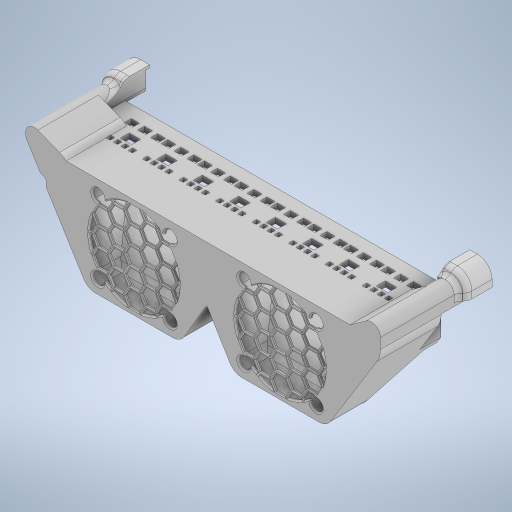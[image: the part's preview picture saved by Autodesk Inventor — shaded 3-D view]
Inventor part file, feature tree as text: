
AUTODESK INVENTOR PART (.ipt)
format: ipt  version: 2023.1 (Build 271208000, 208)  size: 5,121,536 bytes
history: native  units: mm
features: reference x62, projected_geometry x51, extrude x44, sketch x44, delete_face x35, other x18, fillet x13, move_body x9, direct_edit x7, chamfer x7, hole x1
ambient origin geometry x8: Origin, YZ Plane, XZ Plane, XY Plane, X Axis, Y Axis, Z Axis, Center Point
bodies: Volumenkörper1 (feature_tree)
feature tree (291):
  extrude  "Extrusion1"  Depth=2.6mm
  extrude  "Extrusion2"  Depth=0.4195mm
  extrude  "Extrusion3"  Depth=8.0mm
  extrude  "Extrusion4"  Depth=2.6mm
  extrude  "Extrusion5"  Depth=0.482959mm
  extrude  "Extrusion6"  Depth=0.4mm
  delete_face  "Fläche löschen1"
  extrude  "Extrusion7"  Depth=9.8mm TaperAngle=0.0deg
  extrude  "Extrusion8"  Depth=3.0mm TaperAngle=0.0deg
  extrude  "Extrusion9"  Depth=40.0mm
  delete_face  "Fläche löschen2"
  delete_face  "Fläche löschen3"
  delete_face  "Fläche löschen4"
  extrude  "Extrusion10"  Depth=40.0mm
  delete_face  "Fläche löschen5"
  delete_face  "Fläche löschen6"
  delete_face  "Fläche löschen7"
  extrude  "Extrusion11"  Depth=12.004mm
  delete_face  "Fläche löschen8"
  extrude  "Extrusion12"  Depth=12.131mm
  delete_face  "Fläche löschen9"
  delete_face  "Fläche löschen10"
  delete_face  "Fläche löschen11"
  delete_face  "Fläche löschen12"
  extrude  "Extrusion13"  Depth=2.0mm
  extrude  "Extrusion14"  Depth=12.0mm TaperAngle=0.0deg
  delete_face  "Fläche löschen13"
  direct_edit  "Direktbearbeitung1"
  extrude  "Extrusion15"  Depth=0.2mm
  extrude  "Extrusion16"  Depth=0.2mm
  chamfer  "Fase1"  Distance=12.0mm
  delete_face  "Fläche löschen14"
  delete_face  "Fläche löschen15"
  chamfer  "Fase2"  Distance=10.0mm
  delete_face  "Fläche löschen16"
  chamfer  "Fase3"  Distance=10.0mm
  chamfer  "Fase4"  [1 undecoded]
  extrude  "Extrusion17"  Depth=10.0mm TaperAngle=0.0deg
  extrude  "Extrusion18"  Depth=1.2mm
  delete_face  "Fläche löschen17"
  extrude  "Extrusion19"  Depth=54.3755mm
  delete_face  "Fläche löschen18"
  delete_face  "Fläche löschen19"
  extrude  "Extrusion20"  Depth=10.0mm TaperAngle=0.0deg
  extrude  "Extrusion21"  Depth=10.0mm
  fillet  "Rundung1"  Radius=2.044525mm
  fillet  "Rundung2"  Radius=2.044525mm
  delete_face  "Fläche löschen20"
  delete_face  "Fläche löschen21"
  extrude  "Extrusion22"  Depth=5.0mm TaperAngle=0.0deg
  delete_face  "Fläche löschen22"
  extrude  "Extrusion23"  Depth=40.4mm
  extrude  "Extrusion24"  Depth=40.4mm
  delete_face  "Fläche löschen23"
  extrude  "Extrusion25"  Depth=2.0mm
  delete_face  "Fläche löschen24"
  extrude  "Extrusion26"  Depth=2.0mm
  delete_face  "Fläche löschen25"
  extrude  "Extrusion27"  Depth=2.0mm
  delete_face  "Fläche löschen26"
  direct_edit  "Direktbearbeitung2"
  extrude  "Extrusion28"  TaperAngle=30.0deg  [1 undecoded]
  extrude  "Extrusion29"  TaperAngle=30.0deg  [1 undecoded]
  extrude  "Extrusion30"  TaperAngle=45.0deg  [1 undecoded]
  extrude  "Extrusion31"  Depth=2.0mm
  extrude  "Extrusion32"  Depth=2.0mm
  extrude  "Extrusion33"  Depth=2.0mm
  direct_edit  "Direktbearbeitung3"
  delete_face  "Fläche löschen27"
  extrude  "Extrusion34"  Depth=2.0mm
  delete_face  "Fläche löschen28"
  delete_face  "Fläche löschen29"
  delete_face  "Fläche löschen30"
  delete_face  "Fläche löschen31"
  fillet  "Rundung3"  Radius=4.1mm
  extrude  "Extrusion35"  Depth=2.0mm
  chamfer  "Fase5"  Distance=11.1mm
  extrude  "Extrusion36"  Depth=2.0mm
  delete_face  "Fläche löschen32"
  delete_face  "Fläche löschen33"
  direct_edit  "Direktbearbeitung4"
  extrude  "Extrusion37"  Depth=2.0mm
  fillet  "Rundung4"  Radius=13.5mm
  fillet  "Rundung5"  Radius=16.4mm
  fillet  "Rundung6"  Radius=15.2mm
  fillet  "Rundung7"  Radius=8.2mm
  fillet  "Rundung8"  Radius=7.0mm
  fillet  "Rundung9"  Radius=0.0mm
  chamfer  "Fase7"  Distance=1.2mm
  extrude  "Extrusion38"  Depth=2.0mm
  sketch  "Skizze44"  dims[d78=10.0mm d79=0.0mm d80=10.0mm d81=0.0mm]
  extrude  "Extrusion39"  Depth=2.0mm
  extrude  "Extrusion40"  Depth=2.0mm
  direct_edit  "Direktbearbeitung5"
  chamfer  "Fase8"  Distance=17.6mm
  fillet  "Rundung10"  Radius=19.7279mm
  delete_face  "Fläche löschen34"
  delete_face  "Fläche löschen35"
  fillet  "Rundung11"  Radius=19.3mm
  fillet  "Rundung12"  Radius=12.3mm
  extrude  "Extrusion41"  Depth=2.0mm
  extrude  "Extrusion42"  Depth=2.0mm
  direct_edit  "Direktbearbeitung6"
  hole  "Bohrung1"  [1 undecoded]
  direct_edit  "Direktbearbeitung7"
  extrude  "Extrusion43"  Depth=2.0mm
  fillet  "Rundung13"  Radius=5.3mm
  extrude  "Extrusion44"  Depth=2.0mm
  sketch  "Skizze1"  dims[d0=8.8mm d1=0.0mm d4=2.6mm]
  reference  "Referenz1"
  reference  "Referenz2"
  reference  "Referenz3"
  reference  "Referenz4"
  reference  "Referenz5"
  reference  "Referenz6"
  reference  "Referenz7"
  reference  "Referenz8"
  reference  "Referenz9"
  reference  "Referenz10"
  reference  "Referenz11"
  reference  "Referenz12"
  reference  "Referenz13"
  sketch  "Skizze2"  dims[d5=0.4195mm d6=0.4195mm]
  reference  "Referenz14"
  reference  "Referenz15"
  projected_geometry  "Projizierte Kontur1"
  reference  "Referenz16"
  reference  "Referenz17"
  reference  "Referenz18"
  reference  "Referenz19"
  sketch  "Skizze3"  dims[d7=5.999988mm d8=8.0mm]
  projected_geometry  "Projizierte Kontur2"
  reference  "Referenz20"
  reference  "Referenz21"
  reference  "Referenz22"
  reference  "Referenz23"
  reference  "Referenz24"
  reference  "Referenz25"
  sketch  "Skizze4"  dims[d9=8.0mm d10=2.6mm]
  projected_geometry  "Projizierte Kontur3"
  reference  "Referenz26"
  reference  "Referenz27"
  reference  "Referenz28"
  reference  "Referenz29"
  sketch  "Skizze5"  dims[d11=0.482959mm d12=0.482959mm]
  projected_geometry  "Projizierte Kontur4"
  projected_geometry  "Projizierte Kontur5"
  projected_geometry  "Projizierte Kontur6"
  projected_geometry  "Projizierte Kontur7"
  sketch  "Skizze7"  dims[d13=0.4mm d14=0.4mm]
  projected_geometry  "Projizierte Kontur8"
  reference  "Referenz30"
  reference  "Referenz31"
  sketch  "Skizze9"  dims[d15=2.6mm d16=9.8mm d17=0.0mm]
  projected_geometry  "Projizierte Kontur9"
  reference  "Referenz34"
  reference  "Referenz35"
  reference  "Referenz36"
  sketch  "Skizze10"  dims[d18=0.4mm d19=3.0mm d20=0.0mm]
  projected_geometry  "Projizierte Kontur10"
  projected_geometry  "Projizierte Kontur11"
  sketch  "Skizze11"  dims[d21=40.0mm d22=40.0mm]
  projected_geometry  "Projizierte Kontur12"
  sketch  "Skizze13"  dims[d23=40.0mm d24=40.0mm]
  projected_geometry  "Projizierte Kontur13"
  sketch  "Skizze14"  dims[d25=12.004mm d26=12.004mm]
  projected_geometry  "Projizierte Kontur14"
  reference  "Referenz37"
  reference  "Referenz38"
  reference  "Referenz39"
  reference  "Referenz40"
  sketch  "Skizze15"  dims[d27=12.131mm d28=12.131mm]
  projected_geometry  "Projizierte Kontur15"
  sketch  "Skizze16"  dims[d29=2.0mm d30=0.492mm]
  projected_geometry  "Projizierte Kontur16"
  projected_geometry  "Projizierte Kontur17"
  sketch  "Skizze17"  dims[d31=0.492mm d32=12.0mm d33=0.0mm]
  projected_geometry  "Projizierte Kontur18"
  reference  "Referenz41"
  reference  "Referenz42"
  reference  "Referenz43"
  reference  "Referenz44"
  reference  "Referenz45"
  sketch  "Skizze18"  dims[d34=0.2mm d35=0.2mm]
  projected_geometry  "Projizierte Kontur19"
  sketch  "Skizze20"  dims[d36=0.2mm d37=0.2mm]
  projected_geometry  "Projizierte Kontur20"
  projected_geometry  "Projizierte Kontur21"
  sketch  "Skizze21"  dims[d38=0.2mm]
  sketch  "Skizze22"  dims[d39=0.2mm]
  projected_geometry  "Projizierte Kontur22"
  projected_geometry  "Projizierte Kontur23"
  sketch  "Skizze23"  dims[d40=0.2mm]
  sketch  "Skizze24"  dims[d41=1.6mm]
  projected_geometry  "Projizierte Kontur24"
  sketch  "Skizze25"  dims[d42=1.6mm]
  projected_geometry  "Projizierte Kontur25"
  projected_geometry  "Projizierte Kontur26"
  sketch  "Skizze27"  dims[d43=1.6mm]
  projected_geometry  "Projizierte Kontur28"
  sketch  "Skizze28"  dims[d44=1.6mm]
  projected_geometry  "Projizierte Kontur29"
  projected_geometry  "Projizierte Kontur30"
  projected_geometry  "Projizierte Kontur31"
  sketch  "Skizze29"  dims[d45=1.6mm]
  projected_geometry  "Projizierte Kontur32"
  sketch  "Skizze30"  dims[d46=1.6mm]
  projected_geometry  "Projizierte Kontur33"
  sketch  "Skizze31"  dims[d47=1.6mm]
  projected_geometry  "Projizierte Kontur34"
  sketch  "Skizze32"  dims[d48=1.6mm d49=12.0mm d50=0.0mm]
  sketch  "Skizze33"  dims[d51=1.0mm]
  projected_geometry  "Projizierte Kontur35"
  sketch  "Skizze34"  dims[d52=4.2mm]
  projected_geometry  "Projizierte Kontur36"
  projected_geometry  "Projizierte Kontur37"
  sketch  "Skizze35"  dims[d53=1.2mm d54=10.0mm d55=0.0mm]
  projected_geometry  "Projizierte Kontur38"
  projected_geometry  "Projizierte Kontur39"
  sketch  "Skizze36"  dims[d61=1.6mm]
  projected_geometry  "Projizierte Kontur40"
  sketch  "Skizze37"  dims[d62=0.292mm]
  projected_geometry  "Projizierte Kontur41"
  projected_geometry  "Projizierte Kontur42"
  sketch  "Skizze38"  dims[d63=0.292mm]
  projected_geometry  "Projizierte Kontur43"
  sketch  "Skizze39"  dims[d64=1.2mm]
  projected_geometry  "Projizierte Kontur44"
  projected_geometry  "Projizierte Kontur45"
  sketch  "Skizze40"  dims[d65=1.2mm d66=10.0mm d67=0.0mm d68=0.0mm d69=0.0mm]
  projected_geometry  "Projizierte Kontur46"
  sketch  "Skizze41"  dims[d70=10.0mm d71=0.0mm d72=10.0mm d73=0.0mm]
  projected_geometry  "Projizierte Kontur47"
  sketch  "Skizze42"  dims[d74=0.0mm d75=1.2mm]
  projected_geometry  "Projizierte Kontur48"
  sketch  "Skizze43"  dims[d76=108.751mm d77=54.3755mm]
  projected_geometry  "Projizierte Kontur49"
  reference  "Referenz47"
  reference  "Referenz48"
  reference  "Referenz49"
  reference  "Referenz50"
  reference  "Referenz51"
  reference  "Referenz52"
  reference  "Referenz53"
  reference  "Referenz54"
  reference  "Referenz55"
  reference  "Referenz56"
  reference  "Referenz57"
  reference  "Referenz58"
  reference  "Referenz59"
  reference  "Referenz60"
  reference  "Referenz61"
  reference  "Referenz62"
  reference  "Referenz63"
  sketch  "Skizze45"  dims[d82=10.0mm d83=0.0mm d84=1.2mm d85=2.044525mm d86=2.044525mm]
  projected_geometry  "Projizierte Kontur50"
  projected_geometry  "Projizierte Kontur51"
  sketch  "Skizze46"  dims[d87=10.0mm d88=0.0mm d89=0.0mm d90=0.0mm d91=5.0mm]
  projected_geometry  "Projizierte Kontur52"
  sketch  "Skizze47"  dims[d92=12.0mm d93=0.0mm d94=40.4mm]
  reference  "Referenz64"
  reference  "Referenz65"
  sketch  "Skizze48"  dims[d95=40.4mm d97=40.4mm]
  sketch  "Skizze49"  dims[d98=0.0mm d99=2.391982mm d100=2.6mm d101=20.0mm d102=30.0deg d103=30.0deg d104=45.0deg d105=40.6558mm d106=1.2mm d107=4.1mm d108=2.9mm d109=4.1mm d110=5.3mm d111=11.1mm d112=12.3mm d113=12.3mm d114=13.5mm d115=16.4mm d116=15.2mm d117=8.2mm d118=7.0mm d119=0.0mm d120=1.2mm d121=8.2mm d122=9.4mm d123=16.4mm d124=17.6mm d125=19.7279mm d126=19.3mm d127=12.3mm d128=11.1mm d129=4.1mm d130=2.9mm d131=4.1mm d132=5.3mm d133=12.3mm d134=13.5mm d135=20.5mm d136=20.9279mm d137=16.4mm d138=15.2mm d139=8.2mm d140=7.0mm d141=0.0mm d142=1.2mm d143=8.2mm d144=9.4mm d145=16.4mm d146=17.6mm d147=12.3mm d148=13.5mm d149=11.1mm d150=12.3mm d151=4.1mm d152=2.9mm d153=4.1mm d154=5.3mm d155=0.0mm d156=1.2mm d157=4.1mm d158=2.9mm d159=1.2mm d160=5.3mm d161=0.0mm d162=4.1mm d163=8.2mm d164=12.3mm d165=16.4mm d166=1.2mm d167=5.3mm d168=9.4mm d169=13.5mm d170=17.6mm d171=4.1mm d172=8.2mm d173=12.3mm d174=16.4mm d175=20.5mm d176=5.3mm d177=9.4mm d178=13.5mm d179=17.6mm d180=21.7mm d181=12.3mm d182=16.4mm d183=20.5mm d184=24.6mm d185=28.7mm d186=13.5mm d187=17.6mm d188=21.7mm d189=25.8mm d190=29.9mm d191=16.4mm d192=20.5mm d193=24.6mm d194=28.7mm d195=32.8mm d196=17.6mm d197=21.7mm d198=25.8mm d199=29.9mm d200=34.0mm d201=28.7mm d202=32.8mm d203=36.9mm d204=29.9mm d205=34.0mm d206=4.1mm d207=1.2mm d208=2.9mm d209=5.3mm d210=12.3mm d211=8.2mm d212=4.1mm d213=0.0mm d214=16.4mm d215=13.5mm d216=9.4mm d217=5.3mm d218=1.2mm d219=17.6mm d220=4.1mm d221=20.5mm d222=16.4mm d223=12.3mm d224=8.2mm d225=5.3mm d226=21.7mm d227=17.6mm d228=13.5mm d229=9.4mm d230=24.6mm d231=20.5mm d232=16.4mm d233=12.3mm d234=28.7mm d235=25.8mm d236=21.7mm d237=17.6mm d238=13.5mm d239=29.9mm d240=16.4mm d241=32.8mm d242=28.7mm d243=24.6mm d244=20.5mm d245=17.6mm d246=34.0mm d247=29.9mm d248=25.8mm d249=21.7mm d250=28.7mm d251=36.9mm d252=32.8mm d253=29.9mm d254=34.0mm d255=3.592392mm d256=0.0mm d257=3.592392mm d258=3.592392mm d259=0.0mm d260=3.592392mm d261=9.572437mm d262=8.363481mm d263=0.10481mm d264=25.260409mm d265=0.336902mm d266=0.336902mm d267=4.2624mm d268=15.4655mm d269=4.2624mm d270=16.6655mm d271=33.794072mm d272=33.794072mm d273=36.334277mm d274=36.334277mm d275=38.3558mm d276=18.6279mm d277=0.1279mm d278=0.1279mm d279=1.2mm d280=0.6mm d281=2.0mm d282=0.0mm d283=0.6mm d284=2.0mm d285=45.0deg d286=0.4mm d287=2.0mm d288=45.0deg d289=0.6mm d290=2.0mm d291=45.0deg d292=0.4mm d293=2.0mm d294=45.0deg d295=0.0mm d296=0.0mm d297=10.0mm d298=0.0mm d300=12.0mm d301=1.2mm d302=10.0mm d303=0.0mm d304=0.0mm d305=0.0mm d306=3.0mm d307=0.0mm d308=5.0mm d309=6.6mm d310=3.0mm d311=0.0mm d312=10.0mm d313=0.0mm d314=10.0mm d315=0.0mm d316=10.0mm d317=0.0mm d318=0.0mm d319=0.0mm d320=10.0mm d321=0.0mm d322=0.0mm d323=0.0mm d324=5.0mm d325=10.0mm d326=0.0mm d327=10.0mm d328=0.0mm d329=10.0mm d330=0.0mm d331=10.0mm d332=0.0mm d333=1.2mm d334=10.0mm d335=0.0mm d336=10.0mm d337=0.0mm d338=0.0mm d339=0.0mm d340=1.75mm d341=10.0mm d342=0.0mm d343=0.4mm d344=2.0mm d345=0.0mm d346=0.6mm d347=2.0mm d348=45.0deg d349=1.0mm d350=0.0mm d351=0.0mm d352=0.0mm d353=1.75mm d354=1.0mm d355=0.0mm d356=2.0mm d357=1.0mm d358=0.4mm d359=10.0mm d360=5.0mm d361=2.0mm d365=0.4mm d366=2.0mm d367=45.0deg d368=5.6mm d369=3.0mm d370=3.6mm d371=3.6mm d372=3.6mm d373=2.220006mm d374=2.220006mm d375=3.6mm d376=3.6mm d377=3.6mm d378=2.220006mm d379=2.220006mm d380=3.6mm d381=3.6mm d382=3.6mm d383=2.220006mm d384=2.220006mm d385=3.6mm d386=3.6mm d387=3.6mm d388=2.220006mm d389=2.220006mm d390=3.6mm d391=3.6mm d392=3.6mm d393=2.220006mm d394=2.220006mm d395=3.6mm d396=3.6mm d397=3.6mm d398=2.220006mm d399=2.220006mm d400=3.6mm d401=3.6mm d402=3.6mm d403=2.220006mm d404=2.220006mm d425=3.6mm d426=3.6mm d427=3.6mm d428=2.220006mm d429=2.220006mm d430=0.4mm d431=0.0mm d432=0.3mm d433=0.3mm d434=0.3mm d435=0.3mm d437=0.3mm d438=1.2mm d439=1.2mm d440=1.2mm d441=1.2mm d443=1.2mm d444=10.0mm d445=0.0mm d446=1.6mm d447=0.0mm d448=0.0mm d449=0.0mm d450=4.0mm d451=3.8mm d452=2.0mm d453=45.0deg d454=4.0mm d455=4.0mm d456=5.2mm d457=5.0mm d458=10.0mm d459=0.0mm d460=6.2mm d461=0.0mm d462=0.0mm d463=0.0mm d464=0.0mm d465=-1.0mm d466=3.3mm d467=6.0mm d468=4.7mm d469=5.0mm d470=90.0deg d471=8.0mm d472=20.594885mm d473=0.0mm d474=0.0mm d475=0.4mm d476=0.0mm d477=0.0mm d478=1.485505mm d479=0.0mm d480=0.0mm d481=1.000006mm d482=0.0mm d483=0.0mm d484=10.0mm d485=3.0mm d486=3.0mm d487=4.0mm d488=5.0mm d489=5.0mm d490=5.0mm d491=5.0mm d492=5.0mm d493=5.0mm d494=5.0mm d495=5.0mm d496=5.120006mm d497=5.120006mm d498=5.120006mm d499=5.120006mm d500=5.120006mm d501=5.120006mm d502=5.120006mm d503=5.120006mm d504=5.120006mm d505=5.120006mm d506=5.120006mm d507=5.120006mm d508=5.120006mm d509=5.120006mm d510=5.120006mm d511=5.120006mm d512=1.0mm d513=2.0mm d514=2.0mm d522=1.8mm d523=2.0mm d524=1.8mm d525=1.8mm d526=1.8mm d527=11.640012mm d528=11.640012mm d529=1.480004mm d530=1.480004mm d531=1.480004mm d532=1.8mm d533=2.0mm d534=1.8mm d535=1.8mm d536=1.8mm d537=11.640012mm d538=1.480004mm d539=1.480004mm d540=1.480004mm d541=2.0mm d542=11.640012mm d543=1.8mm d544=2.0mm d545=1.8mm d546=1.8mm d547=1.8mm d548=11.640012mm d549=1.480004mm d550=1.480004mm d551=1.480004mm d552=2.0mm d553=11.640012mm d554=1.8mm d555=2.0mm d556=1.8mm d557=1.8mm d558=1.8mm d559=11.640012mm d560=1.480004mm d561=1.480004mm d562=1.480004mm d563=2.0mm d564=11.640012mm d565=1.8mm d566=2.0mm d567=1.8mm d568=1.8mm d569=1.8mm d570=11.640012mm d571=1.480004mm d572=1.480004mm d573=1.480004mm d574=2.0mm d575=11.640012mm d576=1.8mm d577=2.0mm d578=1.8mm d579=1.8mm d580=1.8mm d581=11.640012mm d582=1.480004mm d583=1.480004mm d584=1.480004mm d585=2.0mm d586=11.640012mm d587=1.8mm d588=2.0mm d589=1.8mm d590=1.8mm d591=1.8mm d592=11.640012mm d593=1.480004mm d594=1.480004mm d595=1.480004mm d596=2.0mm d597=11.640012mm d598=1.8mm d599=2.0mm d600=1.8mm d601=1.8mm d602=1.8mm d603=11.640012mm d604=1.480004mm d605=1.480004mm d606=1.480004mm d607=2.0mm d608=11.640012mm d609=3.0mm d610=0.0mm]
  other  "<userpath>\Desktop\GitHub\Voron-2-Mods\Mix\Octopus_Pro_FanCase\FanCase_Assembly.iam"
  other  "FanCase_Assembly.iam"
  other  "Octopus_Pro - beta:1"
  other  "COMPONENTS"
  other  "M11"
  other  "M12"
  other  "BOARD_OUTLINE"
  other  "J47"
  other  "XH-4P"
  other  "MOTOR_DRIVER"
  other  "J15"
  other  "254-3X4-1"
  other  "J41"
  other  "IDC2X5P"
  parser-record x1  (decoder bookkeeping rows leaked as tree rows — omitted from the tree; the rows remain in map.json)
  other  "J67"
  other  "HB9500-8P"
  other  "J12"
  move_body  "Verschieben1"
  move_body  "Verschieben2"
  move_body  "Verschieben3"
  move_body  "Verschieben4"
  move_body  "Verschieben5"
  move_body  "Verschieben6"
  move_body  "Verschieben7"
  move_body  "Verschieben8"
  move_body  "Verschieben9"
note: 5 required parameter values undecoded (feature->parameter linkage not recoverable at this tier; creation-order binding heuristic only, values carry confidence <= 0.55)
